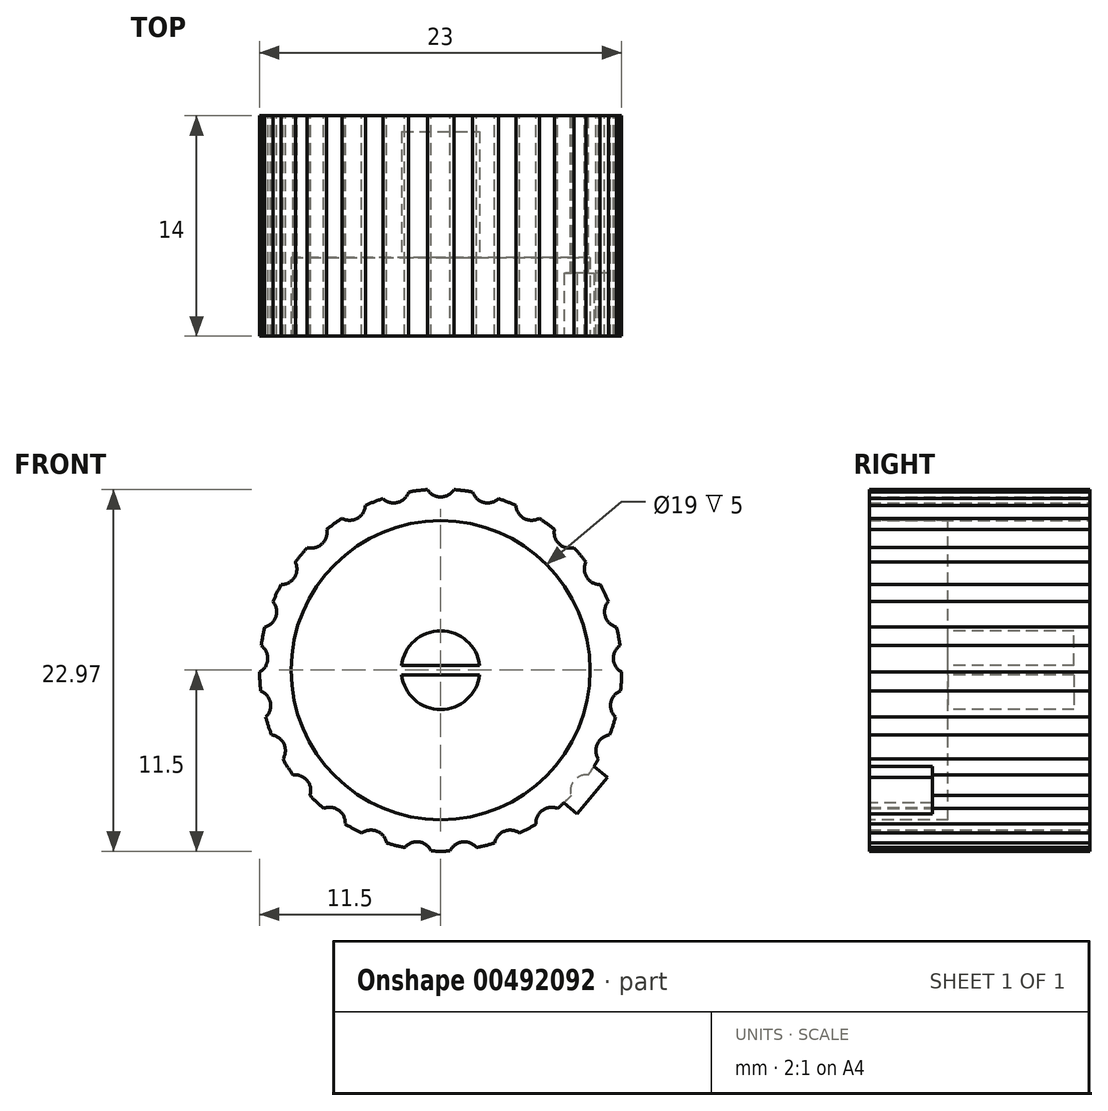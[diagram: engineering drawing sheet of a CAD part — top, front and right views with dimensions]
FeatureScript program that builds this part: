
annotation { "Feature Type Name" : "Feature", "Feature Type Description" : "" }
export const myFeature = defineFeature(function(context is Context, id is Id, definition is map)
    precondition{}
    {
        {
            var Q0;
            Q0=qCreatedBy(makeId("Front.planeOp"),FACE);
            var sketch = newSketch(context, id + "F0", { "sketchPlane" : qUnion([Q0])});
            skCircle(sketch, "E0", {"center": v(0, 0) * mm, "radius": 11.5 * mm});
            skSolve(sketch);
        }
        {
            var Q0;
            Q0=makeQuery(id+"F0.imprint","IMPRINT",FACE,{"disambiguationData":[TD([[makeQuery(id+"F0.imprint","IMPRINT",EDGE,{"derivedFrom":sQuery(id+"F0.wireOp",EDGE,"E0")}),1.0]])]});
            extrude(context, id + "F1", {"entities" : qUnion([Q0]), "oppositeDirection" : true, "depth" : 14 * mm});
        }
        {
            var Q0;
            Q0=makeQuery(id+"F1.opExtrude","CAP_FACE",FACE,{"disambiguationData":[OSD([sQuery(id+"F0.wireOp",EDGE,"E0")])],"isStart":true});
            var sketch = newSketch(context, id + "F2", { "sketchPlane" : qUnion([Q0])});
            skCircle(sketch, "E1", {"center": v(0, 0) * mm, "radius": 9.5 * mm});
            skSolve(sketch);
        }
        {
            var Q0;
            Q0=makeQuery(id+"F2.imprint","IMPRINT",FACE,{"disambiguationData":[TD([[makeQuery(id+"F2.imprint","IMPRINT",EDGE,{"derivedFrom":sQuery(id+"F2.wireOp",EDGE,"E1")}),1.0]])]});
            extrude(context, id + "F3", {"entities" : qUnion([Q0]), "operationType" : NewBodyOperationType.REMOVE, "oppositeDirection" : true, "depth" : 5 * mm});
        }
        {
            var Q0;
            Q0=makeQuery(id+"F3.boolean.opBoolean","COPY",FACE,{"derivedFrom":makeQuery(id+"F3.opExtrude","CAP_FACE",FACE,{"disambiguationData":[OSD([sQuery(id+"F2.wireOp",EDGE,"E1")])],"isStart":false})});
            var sketch = newSketch(context, id + "F4", { "sketchPlane" : qUnion([Q0])});
            skArc(sketch, "E2", {"start": v(2.48, 0.3) * mm, "mid": v(0, 2.5) * mm, "end": v(-2.48, 0.3) * mm});
            skLineSegment(sketch, "E3.bottom", {"start": v(-2.48, 0.3) * mm, "end": v(2.48, 0.3) * mm});
            skLineSegment(sketch, "E3.top", {"start": v(-2.48, -0.3) * mm, "end": v(2.48, -0.3) * mm});
            skLineSegment(sketch, "E3.left", {"start": v(-2.48, 0.3) * mm, "end": v(-2.48, -0.3) * mm, "construction": true});
            skLineSegment(sketch, "E3.right", {"start": v(2.48, 0.3) * mm, "end": v(2.48, -0.3) * mm, "construction": true});
            skLineSegment(sketch, "E4", {"start": v(0, 0) * mm, "end": v(-2.48, 0) * mm, "construction": true});
            skArc(sketch, "E5.trimOffspring", {"start": v(-2.48, -0.3) * mm, "mid": v(0, -2.5) * mm, "end": v(2.48, -0.3) * mm});
            skSolve(sketch);
        }
        {
            var Q0;
            Q0 = qSketchRegion(id + "F4", true);
            extrude(context, id + "F5", {"entities" : qUnion([Q0]), "operationType" : NewBodyOperationType.REMOVE, "oppositeDirection" : true, "depth" : 8 * mm});
        }
        {
            var Q0;
            Q0=makeQuery(id+"F1.opExtrude","CAP_FACE",FACE,{"disambiguationData":[OSD([sQuery(id+"F0.wireOp",EDGE,"E0")])],"isStart":false});
            var sketch = newSketch(context, id + "F6", { "sketchPlane" : qUnion([Q0])});
            skLineSegment(sketch, "E6", {"start": v(0, 0) * mm, "end": v(0, 12) * mm, "construction": true});
            skCircle(sketch, "E7", {"center": v(0, 12) * mm, "radius": 1 * mm});
            skCircle(sketch, "E8.1.0", {"center": v(-2.98, 11.62) * mm, "radius": 1 * mm});
            skCircle(sketch, "E8.2.0", {"center": v(-5.78, 10.52) * mm, "radius": 1 * mm});
            skCircle(sketch, "E8.3.0", {"center": v(-8.21, 8.75) * mm, "radius": 1 * mm});
            skCircle(sketch, "E8.4.0", {"center": v(-10.13, 6.43) * mm, "radius": 1 * mm});
            skCircle(sketch, "E8.5.0", {"center": v(-11.41, 3.7) * mm, "radius": 1 * mm});
            skCircle(sketch, "E8.6.0", {"center": v(-11.98, 0.75) * mm, "radius": 1 * mm});
            skCircle(sketch, "E8.7.0", {"center": v(-11.79, -2.25) * mm, "radius": 1 * mm});
            skCircle(sketch, "E8.8.0", {"center": v(-10.86, -5.1) * mm, "radius": 1 * mm});
            skCircle(sketch, "E8.9.0", {"center": v(-9.25, -7.65) * mm, "radius": 1 * mm});
            skCircle(sketch, "E8.10.0", {"center": v(-7.05, -9.7) * mm, "radius": 1 * mm});
            skCircle(sketch, "E8.11.0", {"center": v(-4.42, -11.16) * mm, "radius": 1 * mm});
            skCircle(sketch, "E8.12.0", {"center": v(-1.5, -11.9) * mm, "radius": 1 * mm});
            skCircle(sketch, "E8.13.0", {"center": v(1.5, -11.9) * mm, "radius": 1 * mm});
            skCircle(sketch, "E8.14.0", {"center": v(4.42, -11.16) * mm, "radius": 1 * mm});
            skCircle(sketch, "E8.15.0", {"center": v(7.05, -9.7) * mm, "radius": 1 * mm});
            skCircle(sketch, "E8.16.0", {"center": v(9.25, -7.65) * mm, "radius": 1 * mm});
            skCircle(sketch, "E8.17.0", {"center": v(10.86, -5.1) * mm, "radius": 1 * mm});
            skCircle(sketch, "E8.18.0", {"center": v(11.79, -2.25) * mm, "radius": 1 * mm});
            skCircle(sketch, "E8.19.0", {"center": v(11.98, 0.75) * mm, "radius": 1 * mm});
            skCircle(sketch, "E8.20.0", {"center": v(11.41, 3.7) * mm, "radius": 1 * mm});
            skCircle(sketch, "E8.21.0", {"center": v(10.13, 6.43) * mm, "radius": 1 * mm});
            skCircle(sketch, "E8.22.0", {"center": v(8.21, 8.75) * mm, "radius": 1 * mm});
            skCircle(sketch, "E8.23.0", {"center": v(5.78, 10.52) * mm, "radius": 1 * mm});
            skCircle(sketch, "E8.24.0", {"center": v(2.98, 11.62) * mm, "radius": 1 * mm});
            skPoint(sketch, "E8.center", {"position": v(0, 0) * mm});
            skSolve(sketch);
        }
        {
            var Q0;
            Q0 = qSketchRegion(id + "F6", true);
            extrude(context, id + "F7", {"entities" : qUnion([Q0]), "operationType" : NewBodyOperationType.REMOVE, "endBound" : BoundingType.THROUGH_ALL, "oppositeDirection" : true, "depth" : 25 * mm});
        }
        {
            var Q0;
            Q0=makeQuery(id+"F1.opExtrude","CAP_FACE",FACE,{"disambiguationData":[OSD([sQuery(id+"F0.wireOp",EDGE,"E0")])],"isStart":true});
            var sketch = newSketch(context, id + "F8", { "sketchPlane" : qUnion([Q0])});
            skPoint(sketch, "E9.endSnap0", {"position": v(0, -11.5) * mm});
            skLineSegment(sketch, "E10", {"start": v(8.48, -7.01) * mm, "end": v(0, 0) * mm, "construction": true});
            skPoint(sketch, "E11", {"position": v(7.7, -6.37) * mm});
            skLineSegment(sketch, "E12.bottom", {"start": v(10.59, -6.81) * mm, "end": v(8.66, -5.22) * mm});
            skLineSegment(sketch, "E12.top", {"start": v(8.68, -9.12) * mm, "end": v(6.75, -7.53) * mm});
            skLineSegment(sketch, "E12.left", {"start": v(10.59, -6.81) * mm, "end": v(8.68, -9.12) * mm});
            skLineSegment(sketch, "E12.right", {"start": v(8.66, -5.22) * mm, "end": v(6.75, -7.53) * mm});
            skSolve(sketch);
        }
        {
            var Q0;
            Q0 = qSketchRegion(id + "F8", true);
            extrude(context, id + "F9", {"entities" : qUnion([Q0]), "operationType" : NewBodyOperationType.ADD, "oppositeDirection" : true, "depth" : 4 * mm});
        }
    });
